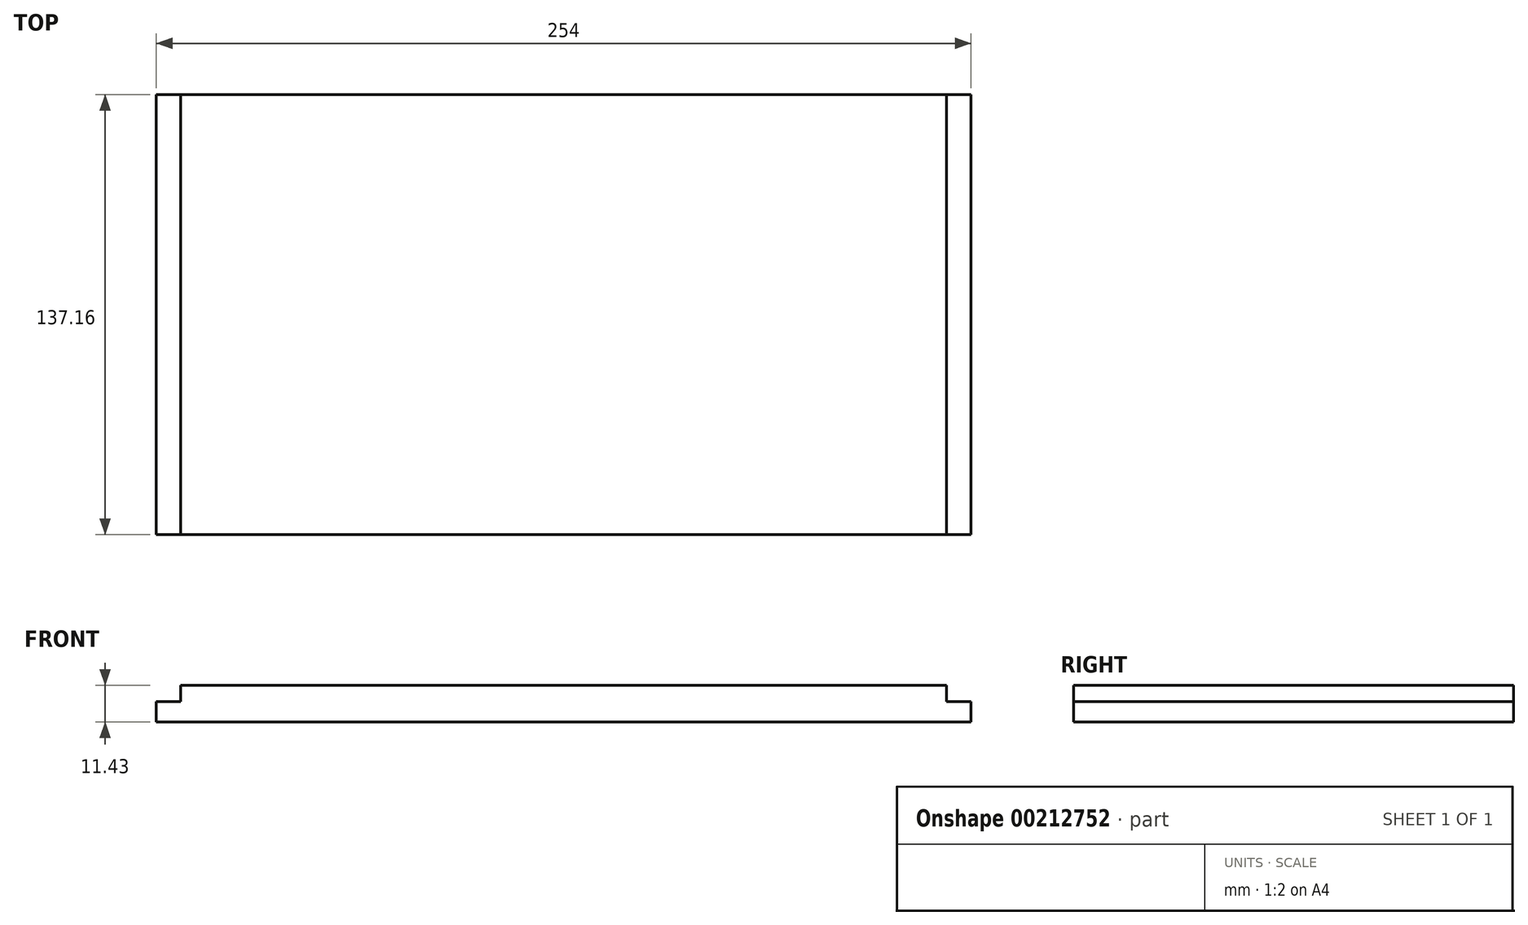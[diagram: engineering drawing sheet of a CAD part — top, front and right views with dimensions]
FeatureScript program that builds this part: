
annotation { "Feature Type Name" : "Feature", "Feature Type Description" : "" }
export const myFeature = defineFeature(function(context is Context, id is Id, definition is map)
    precondition{}
    {
        {
            var Q0;
            Q0=qCreatedBy(makeId("Top.planeOp"),FACE);
            var sketch = newSketch(context, id + "F0", { "sketchPlane" : qUnion([Q0])});
            skLineSegment(sketch, "E0.bottom", {"start": v(-119.38, 68.58) * mm, "end": v(119.38, 68.58) * mm});
            skLineSegment(sketch, "E0.top", {"start": v(-119.38, -68.58) * mm, "end": v(119.38, -68.58) * mm});
            skLineSegment(sketch, "E0.left", {"start": v(-119.38, 68.58) * mm, "end": v(-119.38, -68.58) * mm});
            skLineSegment(sketch, "E0.right", {"start": v(119.38, 68.58) * mm, "end": v(119.38, -68.58) * mm});
            skPoint(sketch, "E0.middle", {"position": v(0, 0) * mm});
            skLineSegment(sketch, "E1.bottom", {"start": v(-127, 68.58) * mm, "end": v(127, 68.58) * mm});
            skLineSegment(sketch, "E1.top", {"start": v(-127, -68.58) * mm, "end": v(127, -68.58) * mm});
            skLineSegment(sketch, "E1.left", {"start": v(-127, 68.58) * mm, "end": v(-127, -68.58) * mm});
            skLineSegment(sketch, "E1.right", {"start": v(127, 68.58) * mm, "end": v(127, -68.58) * mm});
            skSolve(sketch);
        }
        {
            var Q0;
            {var subQ0=sQuery(id+"F0.wireOp",EDGE,"E0.left");Q0=makeQuery(id+"F0.imprint","IMPRINT",FACE,{"disambiguationData":[TD([[makeQuery(id+"F0.imprint","IMPRINT",EDGE,{"derivedFrom":subQ0}),-1.0]])]});}
            var Q1;
            {var subQ0=sQuery(id+"F0.wireOp",EDGE,"E0.left");Q1=makeQuery(id+"F0.imprint","IMPRINT",FACE,{"disambiguationData":[TD([[makeQuery(id+"F0.imprint","IMPRINT",EDGE,{"derivedFrom":subQ0}),1.0]])]});}
            var Q2;
            {var subQ0=sQuery(id+"F0.wireOp",EDGE,"E0.right");Q2=makeQuery(id+"F0.imprint","IMPRINT",FACE,{"disambiguationData":[TD([[makeQuery(id+"F0.imprint","IMPRINT",EDGE,{"derivedFrom":subQ0}),1.0]])]});}
            extrude(context, id + "F1", {"entities" : qUnion([Q0, Q1, Q2]), "depth" : 6.35 * mm});
        }
        {
            var Q0;
            {var subQ0=sQuery(id+"F0.wireOp",EDGE,"E0.left");Q0=makeQuery(id+"F0.imprint","IMPRINT",FACE,{"disambiguationData":[TD([[makeQuery(id+"F0.imprint","IMPRINT",EDGE,{"derivedFrom":subQ0}),1.0]])]});}
            extrude(context, id + "F2", {"entities" : qUnion([Q0]), "operationType" : NewBodyOperationType.ADD, "depth" : 11.43 * mm});
        }
    });
